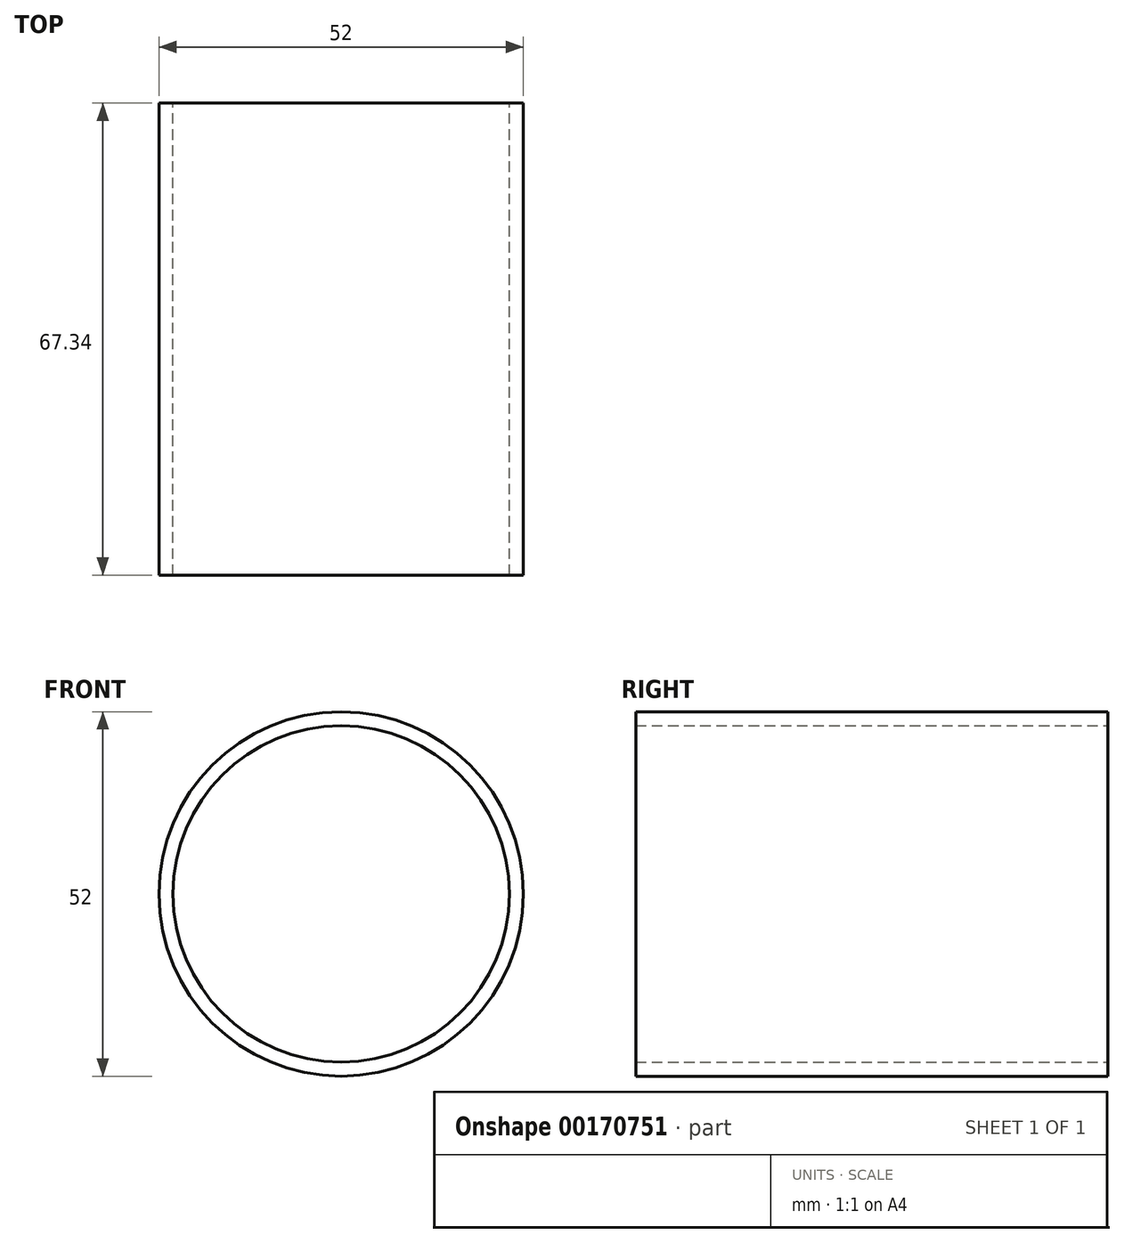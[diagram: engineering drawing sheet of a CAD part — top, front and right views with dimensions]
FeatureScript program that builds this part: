
annotation { "Feature Type Name" : "Feature", "Feature Type Description" : "" }
export const myFeature = defineFeature(function(context is Context, id is Id, definition is map)
    precondition{}
    {
        {
            var Q0;
            Q0=qCreatedBy(makeId("Front.planeOp"),FACE);
            var sketch = newSketch(context, id + "F0", { "sketchPlane" : qUnion([Q0])});
            skCircle(sketch, "E0", {"center": v(0, 0) * mm, "radius": 26 * mm});
            skCircle(sketch, "E1", {"center": v(0, 0) * mm, "radius": 24 * mm});
            skSolve(sketch);
        }
        {
            var Q0;
            Q0=qSketchRegion(id+"F0",true);
            extrude(context, id + "F1", {"entities" : qUnion([Q0]), "flatOperationType" : FlatOperationType.REMOVE, "offsetDistance" : 25 * mm, "depth" : 67.33 * mm, "domain" : OperationDomain.MODEL, "symmetric" : true});
        }
    });
